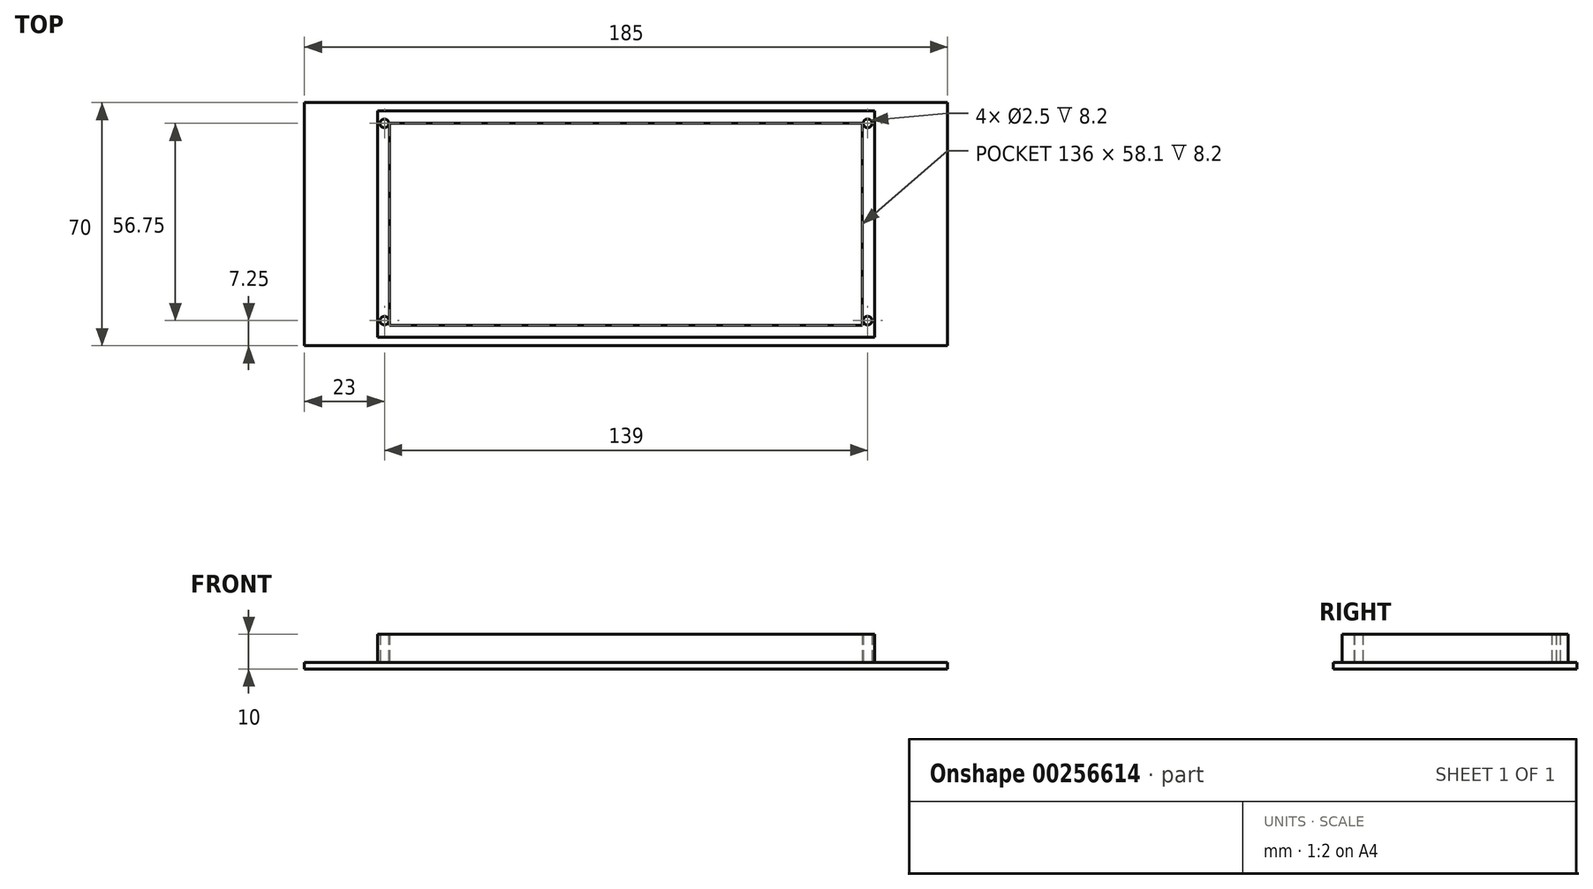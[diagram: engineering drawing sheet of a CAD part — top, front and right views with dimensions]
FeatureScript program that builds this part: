
annotation { "Feature Type Name" : "Feature", "Feature Type Description" : "" }
export const myFeature = defineFeature(function(context is Context, id is Id, definition is map)
    precondition{}
    {
        {
            var Q0;
            Q0=qCreatedBy(makeId("Top.planeOp"),FACE);
            var sketch = newSketch(context, id + "F0", { "sketchPlane" : qUnion([Q0])});
            skLineSegment(sketch, "E0.bottom", {"start": v(67, -28.05) * mm, "end": v(-67, -28.05) * mm, "construction": true});
            skLineSegment(sketch, "E0.top", {"start": v(67, 28.05) * mm, "end": v(-67, 28.05) * mm, "construction": true});
            skLineSegment(sketch, "E0.left", {"start": v(67, -28.05) * mm, "end": v(67, 28.05) * mm, "construction": true});
            skLineSegment(sketch, "E0.right", {"start": v(-67, -28.05) * mm, "end": v(-67, 28.05) * mm, "construction": true});
            skPoint(sketch, "E0.middle", {"position": v(0, 0) * mm});
            skLineSegment(sketch, "E1.bottom", {"start": v(73, -31.25) * mm, "end": v(-73, -31.25) * mm, "construction": true});
            skLineSegment(sketch, "E1.top", {"start": v(73, 31.25) * mm, "end": v(-73, 31.25) * mm, "construction": true});
            skLineSegment(sketch, "E1.left", {"start": v(73, -31.25) * mm, "end": v(73, 31.25) * mm, "construction": true});
            skLineSegment(sketch, "E1.right", {"start": v(-73, -31.25) * mm, "end": v(-73, 31.25) * mm, "construction": true});
            skCircle(sketch, "E2", {"center": v(-69.5, -27.75) * mm, "radius": 1.25 * mm, "construction": true});
            skCircle(sketch, "E3", {"center": v(-69.5, 29) * mm, "radius": 1.25 * mm, "construction": true});
            skCircle(sketch, "E4", {"center": v(69.5, 29) * mm, "radius": 1.25 * mm, "construction": true});
            skCircle(sketch, "E5", {"center": v(69.5, -27.75) * mm, "radius": 1.25 * mm, "construction": true});
            skLineSegment(sketch, "E6.bottom", {"start": v(68, -29.05) * mm, "end": v(-68, -29.05) * mm});
            skLineSegment(sketch, "E6.top", {"start": v(68, 29.05) * mm, "end": v(-68, 29.05) * mm});
            skLineSegment(sketch, "E6.left", {"start": v(68, -29.05) * mm, "end": v(68, 29.05) * mm});
            skLineSegment(sketch, "E6.right", {"start": v(-68, -29.05) * mm, "end": v(-68, 29.05) * mm});
            skLineSegment(sketch, "E7.bottom", {"start": v(92.5, -35) * mm, "end": v(-92.5, -35) * mm});
            skLineSegment(sketch, "E7.top", {"start": v(92.5, 35) * mm, "end": v(-92.5, 35) * mm});
            skLineSegment(sketch, "E7.left", {"start": v(92.5, -35) * mm, "end": v(92.5, 35) * mm});
            skLineSegment(sketch, "E7.right", {"start": v(-92.5, -35) * mm, "end": v(-92.5, 35) * mm});
            skLineSegment(sketch, "E8.0", {"start": v(71.5, -32.55) * mm, "end": v(-71.5, -32.55) * mm});
            skLineSegment(sketch, "E8.1", {"start": v(71.5, -32.55) * mm, "end": v(71.5, 32.55) * mm});
            skLineSegment(sketch, "E8.2", {"start": v(71.5, 32.55) * mm, "end": v(-71.5, 32.55) * mm});
            skLineSegment(sketch, "E8.3", {"start": v(-71.5, -32.55) * mm, "end": v(-71.5, 32.55) * mm});
            skCircle(sketch, "E9", {"center": v(-69.5, 29) * mm, "radius": 1.25 * mm});
            skCircle(sketch, "E10", {"center": v(69.5, 29) * mm, "radius": 1.25 * mm});
            skCircle(sketch, "E11", {"center": v(69.5, -27.75) * mm, "radius": 1.25 * mm});
            skCircle(sketch, "E12", {"center": v(-69.5, -27.75) * mm, "radius": 1.25 * mm});
            skSolve(sketch);
        }
        {
            var Q0;
            Q0=makeQuery(id+"F0.imprint","IMPRINT",FACE,{"disambiguationData":[TD([[makeQuery(id+"F0.imprint","IMPRINT",EDGE,{"derivedFrom":sQuery(id+"F0.wireOp",EDGE,"E6.bottom")}),-1.0]])]});
            var Q1;
            Q1=makeQuery(id+"F0.imprint","IMPRINT",FACE,{"disambiguationData":[TD([[makeQuery(id+"F0.imprint","IMPRINT",EDGE,{"derivedFrom":sQuery(id+"F0.wireOp",EDGE,"E6.bottom")}),1.0]])]});
            var Q2;
            Q2=makeQuery(id+"F0.imprint","IMPRINT",FACE,{"disambiguationData":[TD([[makeQuery(id+"F0.imprint","IMPRINT",EDGE,{"derivedFrom":sQuery(id+"F0.wireOp",EDGE,"E7.bottom")}),-1.0]])]});
            var Q3;
            Q3=makeQuery(id+"F0.imprint","IMPRINT",FACE,{"disambiguationData":[TD([[makeQuery(id+"F0.imprint","IMPRINT",EDGE,{"derivedFrom":sQuery(id+"F0.wireOp",EDGE,"E12")}),1.0]])]});
            var Q4;
            Q4=makeQuery(id+"F0.imprint","IMPRINT",FACE,{"disambiguationData":[TD([[makeQuery(id+"F0.imprint","IMPRINT",EDGE,{"derivedFrom":sQuery(id+"F0.wireOp",EDGE,"E9")}),1.0]])]});
            var Q5;
            Q5=makeQuery(id+"F0.imprint","IMPRINT",FACE,{"disambiguationData":[TD([[makeQuery(id+"F0.imprint","IMPRINT",EDGE,{"derivedFrom":sQuery(id+"F0.wireOp",EDGE,"E10")}),1.0]])]});
            var Q6;
            Q6=makeQuery(id+"F0.imprint","IMPRINT",FACE,{"disambiguationData":[TD([[makeQuery(id+"F0.imprint","IMPRINT",EDGE,{"derivedFrom":sQuery(id+"F0.wireOp",EDGE,"E11")}),1.0]])]});
            extrude(context, id + "F1", {"entities" : qUnion([Q0, Q1, Q2, Q3, Q4, Q5, Q6]), "depth" : 1.8 * mm, "offsetDistance" : 25 * mm});
        }
        {
            var Q0;
            Q0=makeQuery(id+"F0.imprint","IMPRINT",FACE,{"disambiguationData":[TD([[makeQuery(id+"F0.imprint","IMPRINT",EDGE,{"derivedFrom":sQuery(id+"F0.wireOp",EDGE,"E6.bottom")}),1.0]])]});
            extrude(context, id + "F2", {"entities" : qUnion([Q0]), "operationType" : NewBodyOperationType.ADD, "depth" : 10 * mm, "offsetDistance" : 25 * mm});
        }
    });
